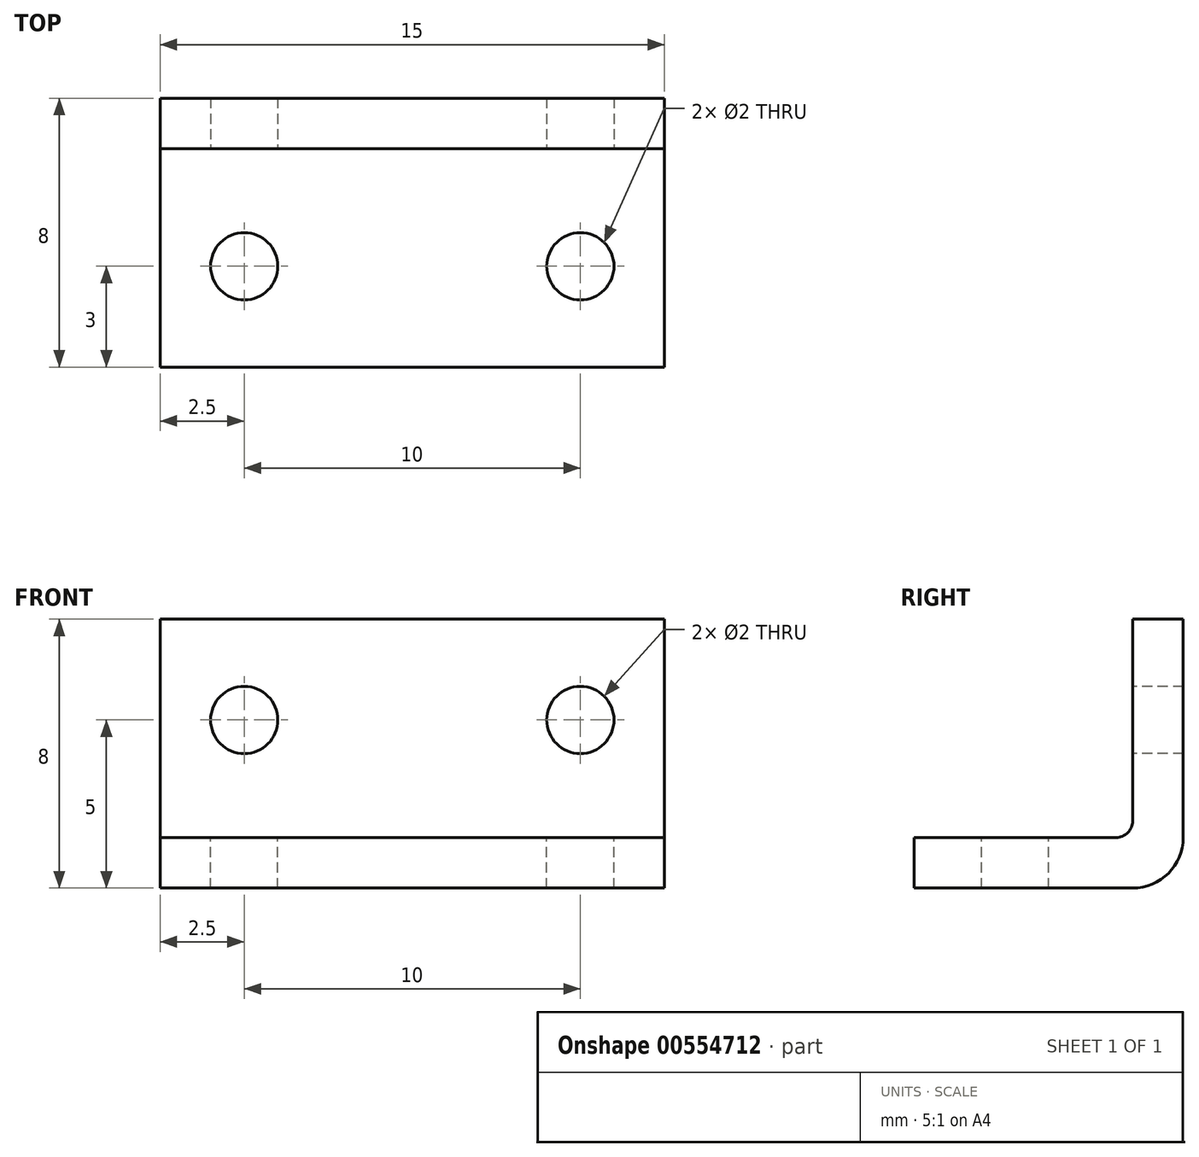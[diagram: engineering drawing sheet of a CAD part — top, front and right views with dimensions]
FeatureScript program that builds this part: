
annotation { "Feature Type Name" : "Feature", "Feature Type Description" : "" }
export const myFeature = defineFeature(function(context is Context, id is Id, definition is map)
    precondition{}
    {
        {
            var Q0;
            Q0=qCreatedBy(makeId("Right.planeOp"),FACE);
            var sketch = newSketch(context, id + "F0", { "sketchPlane" : qUnion([Q0])});
            skLineSegment(sketch, "E0", {"start": v(-1.5, 0) * mm, "end": v(-8, 0) * mm});
            skLineSegment(sketch, "E1", {"start": v(-8, 0) * mm, "end": v(-8, 1.5) * mm});
            skLineSegment(sketch, "E2", {"start": v(-8, 1.5) * mm, "end": v(-2, 1.5) * mm});
            skLineSegment(sketch, "E3", {"start": v(-1.5, 2) * mm, "end": v(-1.5, 8) * mm});
            skLineSegment(sketch, "E4", {"start": v(-1.5, 8) * mm, "end": v(0, 8) * mm});
            skLineSegment(sketch, "E5", {"start": v(0, 8) * mm, "end": v(0, 1.5) * mm});
            skPoint(sketch, "E6.visualSharp", {"position": v(-1.5, 1.5) * mm});
            skArc(sketch, "E6.filletArc", {"start": v(-2, 1.5) * mm, "mid": v(-1.65, 1.65) * mm, "end": v(-1.5, 2) * mm});
            skPoint(sketch, "E7.visualSharp", {"position": v(0, 0) * mm});
            skArc(sketch, "E7.filletArc", {"start": v(-1.5, 0) * mm, "mid": v(-0.44, 0.44) * mm, "end": v(0, 1.5) * mm});
            skSolve(sketch);
        }
        {
            var Q0;
            Q0 = qSketchRegion(id + "F0", true);
            extrude(context, id + "F1", {"entities" : qUnion([Q0]), "endBound" : BoundingType.SYMMETRIC, "depth" : 15 * mm, "offsetDistance" : 25 * mm});
        }
        {
            var Q0;
            Q0=makeQuery(id+"F1.opExtrude","SWEPT_FACE",FACE,{"disambiguationData":[OSD([sQuery(id+"F0.wireOp",EDGE,"E2")])]});
            var sketch = newSketch(context, id + "F2", { "sketchPlane" : qUnion([Q0])});
            skPoint(sketch, "E8", {"position": v(5, -5) * mm});
            skPoint(sketch, "E9", {"position": v(-5, -5) * mm});
            skCircle(sketch, "E10", {"center": v(-5, -5) * mm, "radius": 1 * mm});
            skCircle(sketch, "E11", {"center": v(5, -5) * mm, "radius": 1 * mm});
            skSolve(sketch);
        }
        {
            var Q0;
            Q0=makeQuery(id+"F1.opExtrude","SWEPT_FACE",FACE,{"disambiguationData":[OSD([sQuery(id+"F0.wireOp",EDGE,"E3")])]});
            var sketch = newSketch(context, id + "F3", { "sketchPlane" : qUnion([Q0])});
            skPoint(sketch, "E12", {"position": v(-5, 5) * mm});
            skPoint(sketch, "E13", {"position": v(5, 5) * mm});
            skCircle(sketch, "E14", {"center": v(-5, 5) * mm, "radius": 1 * mm});
            skCircle(sketch, "E15", {"center": v(5, 5) * mm, "radius": 1 * mm});
            skSolve(sketch);
        }
        {
            var Q0;
            Q0=makeQuery(id+"F3.imprint","IMPRINT",FACE,{"disambiguationData":[TD([[makeQuery(id+"F3.imprint","IMPRINT",EDGE,{"derivedFrom":sQuery(id+"F3.wireOp",EDGE,"E14")}),1.0]])]});
            var Q1;
            Q1=makeQuery(id+"F3.imprint","IMPRINT",FACE,{"disambiguationData":[TD([[makeQuery(id+"F3.imprint","IMPRINT",EDGE,{"derivedFrom":sQuery(id+"F3.wireOp",EDGE,"E15")}),1.0]])]});
            extrude(context, id + "F4", {"entities" : qUnion([Q0, Q1]), "operationType" : NewBodyOperationType.REMOVE, "oppositeDirection" : true, "depth" : 1.5 * mm, "offsetDistance" : 25 * mm});
        }
        {
            var Q0;
            Q0=makeQuery(id+"F2.imprint","IMPRINT",FACE,{"disambiguationData":[TD([[makeQuery(id+"F2.imprint","IMPRINT",EDGE,{"derivedFrom":sQuery(id+"F2.wireOp",EDGE,"E11")}),1.0]])]});
            var Q1;
            Q1=makeQuery(id+"F2.imprint","IMPRINT",FACE,{"disambiguationData":[TD([[makeQuery(id+"F2.imprint","IMPRINT",EDGE,{"derivedFrom":sQuery(id+"F2.wireOp",EDGE,"E10")}),1.0]])]});
            extrude(context, id + "F5", {"entities" : qUnion([Q0, Q1]), "operationType" : NewBodyOperationType.REMOVE, "oppositeDirection" : true, "depth" : 1.5 * mm, "offsetDistance" : 25 * mm});
        }
    });
